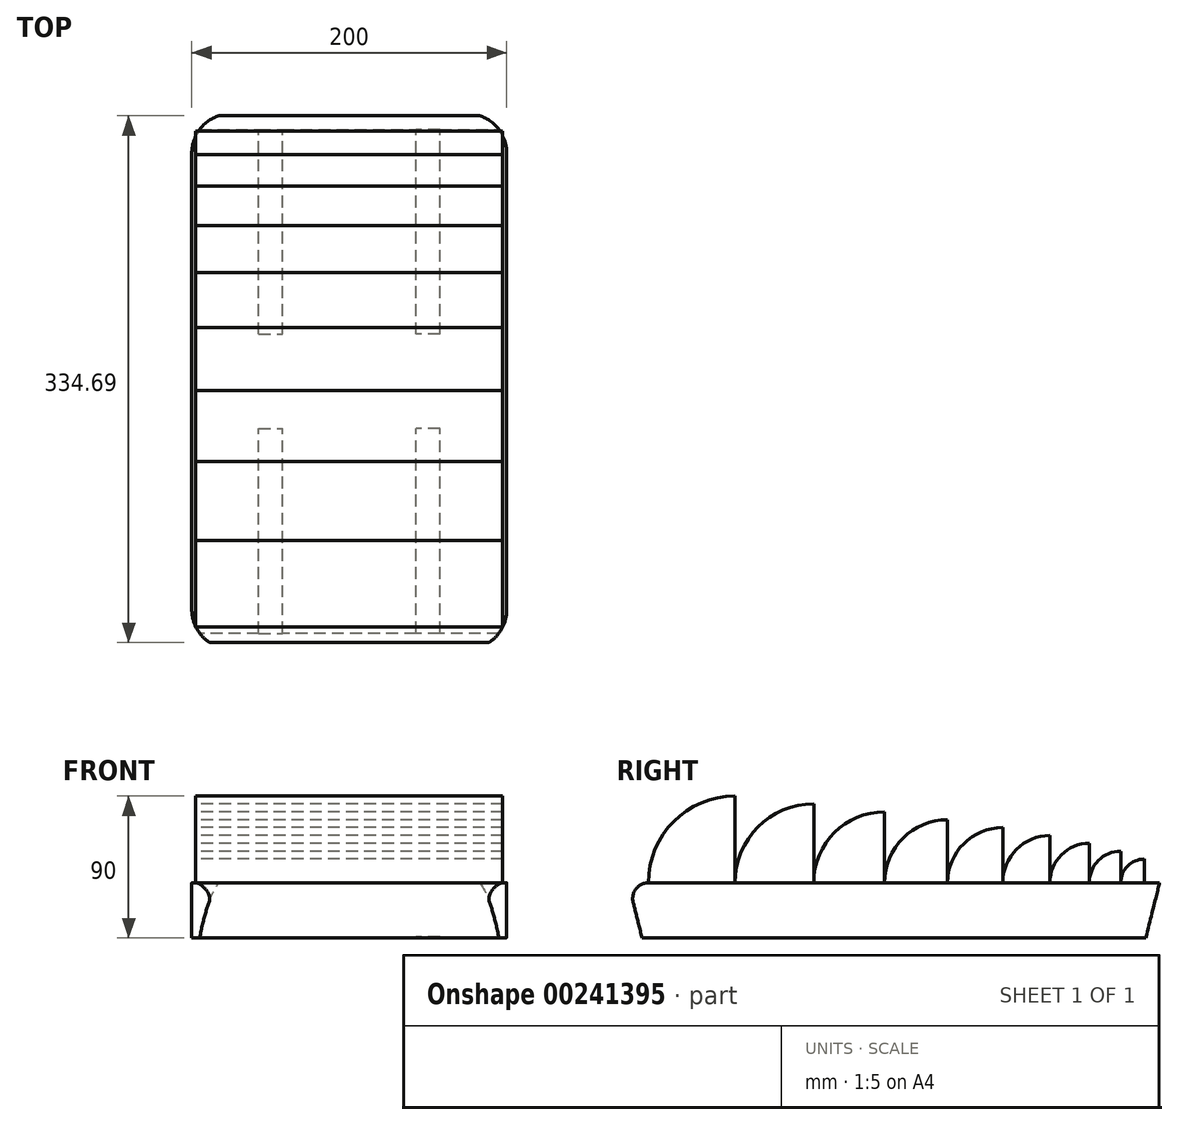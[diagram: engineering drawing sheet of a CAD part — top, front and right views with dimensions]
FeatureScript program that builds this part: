
annotation { "Feature Type Name" : "Feature", "Feature Type Description" : "" }
export const myFeature = defineFeature(function(context is Context, id is Id, definition is map)
    precondition{}
    {
        {
            var Q0;
            Q0=qCreatedBy(makeId("Top.planeOp"),FACE);
            var sketch = newSketch(context, id + "F0", { "sketchPlane" : qUnion([Q0])});
            skLineSegment(sketch, "E0.bottom", {"start": v(-100, 170) * mm, "end": v(100, 170) * mm});
            skLineSegment(sketch, "E0.top", {"start": v(-100, -170) * mm, "end": v(100, -170) * mm});
            skLineSegment(sketch, "E0.left", {"start": v(-100, 170) * mm, "end": v(-100, -170) * mm});
            skLineSegment(sketch, "E0.right", {"start": v(100, 170) * mm, "end": v(100, -170) * mm});
            skPoint(sketch, "E0.middle", {"position": v(0, 0) * mm});
            skSolve(sketch);
        }
        {
            var Q0;
            Q0 = qSketchRegion(id + "F0", true);
            extrude(context, id + "F1", {"entities" : qUnion([Q0]), "depth" : 35 * mm});
        }
        {
            var Q0;
            Q0=makeQuery(id+"F1.opExtrude","CAP_FACE",FACE,{"disambiguationData":[OSD([sQuery(id+"F0.wireOp",EDGE,"E0.bottom"),sQuery(id+"F0.wireOp",EDGE,"E0.top"),sQuery(id+"F0.wireOp",EDGE,"E0.left"),sQuery(id+"F0.wireOp",EDGE,"E0.right")])],"isStart":true});
            var sketch = newSketch(context, id + "F2", { "sketchPlane" : qUnion([Q0])});
            skLineSegment(sketch, "E1.bottom", {"start": v(-57.5, 160) * mm, "end": v(-42.5, 160) * mm});
            skLineSegment(sketch, "E1.top", {"start": v(-57.5, 30) * mm, "end": v(-42.5, 30) * mm});
            skLineSegment(sketch, "E1.left", {"start": v(-57.5, 160) * mm, "end": v(-57.5, 30) * mm});
            skLineSegment(sketch, "E1.right", {"start": v(-42.5, 160) * mm, "end": v(-42.5, 30) * mm});
            skLineSegment(sketch, "E2.bottom", {"start": v(57.5, 160) * mm, "end": v(42.5, 160) * mm});
            skLineSegment(sketch, "E2.top", {"start": v(57.5, 30) * mm, "end": v(42.5, 30) * mm});
            skLineSegment(sketch, "E2.left", {"start": v(57.5, 160) * mm, "end": v(57.5, 30) * mm});
            skLineSegment(sketch, "E2.right", {"start": v(42.5, 160) * mm, "end": v(42.5, 30) * mm});
            skLineSegment(sketch, "E3.bottom", {"start": v(-57.5, -30) * mm, "end": v(-42.5, -30) * mm});
            skLineSegment(sketch, "E3.top", {"start": v(-57.5, -160) * mm, "end": v(-42.5, -160) * mm});
            skLineSegment(sketch, "E3.left", {"start": v(-57.5, -30) * mm, "end": v(-57.5, -160) * mm});
            skLineSegment(sketch, "E3.right", {"start": v(-42.5, -30) * mm, "end": v(-42.5, -160) * mm});
            skLineSegment(sketch, "E4.bottom", {"start": v(57.5, -30) * mm, "end": v(42.5, -30) * mm});
            skLineSegment(sketch, "E4.top", {"start": v(57.5, -160) * mm, "end": v(42.5, -160) * mm});
            skLineSegment(sketch, "E4.left", {"start": v(57.5, -30) * mm, "end": v(57.5, -160) * mm});
            skLineSegment(sketch, "E4.right", {"start": v(42.5, -30) * mm, "end": v(42.5, -160) * mm});
            skSolve(sketch);
        }
        {
            var Q0;
            Q0 = qSketchRegion(id + "F2", true);
            extrude(context, id + "F3", {"entities" : qUnion([Q0]), "operationType" : NewBodyOperationType.REMOVE, "oppositeDirection" : true, "depth" : .5 * mm});
        }
        {
            var Q0;
            Q0=makeQuery(id+"F1.opExtrude","SWEPT_EDGE",EDGE,{"disambiguationData":[OSD([sQuery(id+"F0.wireOp",EDGE,"E0.top"),sQuery(id+"F0.wireOp",EDGE,"E0.right")])]});
            var Q1;
            Q1=makeQuery(id+"F1.opExtrude","SWEPT_EDGE",EDGE,{"disambiguationData":[OSD([sQuery(id+"F0.wireOp",EDGE,"E0.top"),sQuery(id+"F0.wireOp",EDGE,"E0.left")])]});
            var Q2;
            Q2=makeQuery(id+"F1.opExtrude","SWEPT_EDGE",EDGE,{"disambiguationData":[OSD([sQuery(id+"F0.wireOp",EDGE,"E0.bottom"),sQuery(id+"F0.wireOp",EDGE,"E0.right")])]});
            var Q3;
            Q3=makeQuery(id+"F1.opExtrude","SWEPT_EDGE",EDGE,{"disambiguationData":[OSD([sQuery(id+"F0.wireOp",EDGE,"E0.bottom"),sQuery(id+"F0.wireOp",EDGE,"E0.left")])]});
            fillet(context, id + "F4", {"entities" : qUnion([Q0, Q1, Q2, Q3]), "radius" : 25 * mm, "tangentPropagation" : true, "allowEdgeOverflow" : false});
        }
        {
            var Q0;
            Q0=makeQuery(id+"F1.opExtrude","CAP_EDGE",EDGE,{"disambiguationData":[OSD([sQuery(id+"F0.wireOp",EDGE,"E0.top")])],"isStart":true});
            var Q1;
            Q1=makeQuery(id+"F1.opExtrude","CAP_EDGE",EDGE,{"disambiguationData":[OSD([sQuery(id+"F0.wireOp",EDGE,"E0.bottom")])],"isStart":true});
            chamfer(context, id + "F5", {"entities" : qUnion([Q0, Q1]), "chamferType" : ChamferType.TWO_OFFSETS, "width1" : 40 * mm, "oppositeDirection" : false, "width2" : 10 * mm});
        }
        {
            var Q0;
            {var subQ0=sQuery(id+"F0.wireOp",EDGE,"E0.top");Q0=makeQuery(id+"F5.opChamfer","BLEND_EDGE",EDGE,{"blendedFrom":[makeQuery(id+"F1.opExtrude","CAP_EDGE",EDGE,{"disambiguationData":[OSD([subQ0])],"isStart":true}),makeQuery(id+"F1.opExtrude","CAP_FACE",FACE,{"disambiguationData":[OSD([sQuery(id+"F0.wireOp",EDGE,"E0.bottom"),subQ0,sQuery(id+"F0.wireOp",EDGE,"E0.left"),sQuery(id+"F0.wireOp",EDGE,"E0.right")])],"isStart":false})],"blendedInto":[makeQuery(id+"F1.opExtrude","CAP_FACE",FACE,{"disambiguationData":[OSD([sQuery(id+"F0.wireOp",EDGE,"E0.bottom"),subQ0,sQuery(id+"F0.wireOp",EDGE,"E0.left"),sQuery(id+"F0.wireOp",EDGE,"E0.right")])],"isStart":false})]});}
            fillet(context, id + "F6", {"entities" : qUnion([Q0]), "radius" : 10 * mm, "tangentPropagation" : true, "allowEdgeOverflow" : false});
        }
        {
            var Q0;
            Q0=qCreatedBy(makeId("Right.planeOp"),FACE);
            var sketch = newSketch(context, id + "F7", { "sketchPlane" : qUnion([Q0])});
            skLineSegment(sketch, "E5.bottom", {"start": v(-100.94, 35) * mm, "end": v(-155.94, 35) * mm});
            skLineSegment(sketch, "E5.top", {"start": v(-100.94, 90) * mm, "end": v(-100.94, 90) * mm});
            skLineSegment(sketch, "E5.left", {"start": v(-100.94, 35) * mm, "end": v(-100.94, 90) * mm});
            skLineSegment(sketch, "E5.right", {"start": v(-155.94, 35) * mm, "end": v(-155.94, 35) * mm});
            skPoint(sketch, "E6.visualSharp", {"position": v(-155.94, 90) * mm});
            skArc(sketch, "E6.filletArc", {"start": v(-100.94, 90) * mm, "mid": v(-139.83, 73.9) * mm, "end": v(-155.94, 35) * mm});
            skLineSegment(sketch, "E7.bottom", {"start": v(-50.94, 35) * mm, "end": v(-100.94, 35) * mm});
            skLineSegment(sketch, "E7.left", {"start": v(-50.94, 35) * mm, "end": v(-50.94, 85) * mm});
            skArc(sketch, "E8", {"start": v(-50.94, 85) * mm, "mid": v(-86.3, 70.36) * mm, "end": v(-100.94, 35) * mm});
            skLineSegment(sketch, "E9.bottom", {"start": v(-50.94, 35) * mm, "end": v(-5.94, 35) * mm});
            skLineSegment(sketch, "E9.right", {"start": v(-5.94, 35) * mm, "end": v(-5.94, 80) * mm});
            skArc(sketch, "E10", {"start": v(-5.94, 80) * mm, "mid": v(-37.76, 66.82) * mm, "end": v(-50.94, 35) * mm});
            skLineSegment(sketch, "E11.bottom", {"start": v(-5.94, 35) * mm, "end": v(34.06, 35) * mm});
            skLineSegment(sketch, "E11.top", {"start": v(-5.94, 75) * mm, "end": v(34.06, 75) * mm});
            skLineSegment(sketch, "E11.left", {"start": v(-5.94, 35) * mm, "end": v(-5.94, 75) * mm});
            skLineSegment(sketch, "E11.right", {"start": v(34.06, 35) * mm, "end": v(34.06, 75) * mm});
            skArc(sketch, "E12", {"start": v(34.06, 75) * mm, "mid": v(5.77, 63.28) * mm, "end": v(-5.94, 35) * mm});
            skLineSegment(sketch, "E13.bottom", {"start": v(34.06, 35) * mm, "end": v(69.06, 35) * mm});
            skLineSegment(sketch, "E13.top", {"start": v(34.06, 70) * mm, "end": v(69.06, 70) * mm});
            skLineSegment(sketch, "E13.left", {"start": v(34.06, 35) * mm, "end": v(34.06, 70) * mm});
            skLineSegment(sketch, "E13.right", {"start": v(69.06, 35) * mm, "end": v(69.06, 70) * mm});
            skLineSegment(sketch, "E14.bottom", {"start": v(69.06, 35) * mm, "end": v(99.06, 35) * mm});
            skLineSegment(sketch, "E14.top", {"start": v(69.06, 65) * mm, "end": v(99.06, 65) * mm});
            skLineSegment(sketch, "E14.left", {"start": v(69.06, 35) * mm, "end": v(69.06, 65) * mm});
            skLineSegment(sketch, "E14.right", {"start": v(99.06, 35) * mm, "end": v(99.06, 65) * mm});
            skLineSegment(sketch, "E15.bottom", {"start": v(99.06, 35) * mm, "end": v(124.06, 35) * mm});
            skLineSegment(sketch, "E15.top", {"start": v(99.06, 60) * mm, "end": v(124.06, 60) * mm});
            skLineSegment(sketch, "E15.left", {"start": v(99.06, 35) * mm, "end": v(99.06, 60) * mm});
            skLineSegment(sketch, "E15.right", {"start": v(124.06, 35) * mm, "end": v(124.06, 60) * mm});
            skLineSegment(sketch, "E16.bottom", {"start": v(124.06, 35) * mm, "end": v(144.06, 35) * mm});
            skLineSegment(sketch, "E16.top", {"start": v(124.06, 55) * mm, "end": v(144.06, 55) * mm});
            skLineSegment(sketch, "E16.left", {"start": v(124.06, 35) * mm, "end": v(124.06, 55) * mm});
            skLineSegment(sketch, "E16.right", {"start": v(144.06, 35) * mm, "end": v(144.06, 55) * mm});
            skLineSegment(sketch, "E17.bottom", {"start": v(144.06, 35) * mm, "end": v(159.06, 35) * mm});
            skLineSegment(sketch, "E17.top", {"start": v(144.06, 50) * mm, "end": v(159.06, 50) * mm});
            skLineSegment(sketch, "E17.left", {"start": v(144.06, 35) * mm, "end": v(144.06, 50) * mm});
            skLineSegment(sketch, "E17.right", {"start": v(159.06, 35) * mm, "end": v(159.06, 50) * mm});
            skArc(sketch, "E18", {"start": v(69.06, 70) * mm, "mid": v(44.3, 59.75) * mm, "end": v(34.06, 35) * mm});
            skArc(sketch, "E19", {"start": v(99.06, 65) * mm, "mid": v(77.84, 56.21) * mm, "end": v(69.06, 35) * mm});
            skArc(sketch, "E20", {"start": v(124.06, 60) * mm, "mid": v(106.38, 52.68) * mm, "end": v(99.06, 35) * mm});
            skArc(sketch, "E21", {"start": v(144.06, 55) * mm, "mid": v(129.92, 49.14) * mm, "end": v(124.06, 35) * mm});
            skArc(sketch, "E22", {"start": v(159.06, 50) * mm, "mid": v(148.45, 45.6) * mm, "end": v(144.06, 35) * mm});
            skSolve(sketch);
        }
        {
            var Q0;
            Q0=makeQuery(id+"F7.imprint","IMPRINT",FACE,{"disambiguationData":[TD([[makeQuery(id+"F7.imprint","IMPRINT",EDGE,{"derivedFrom":sQuery(id+"F7.wireOp",EDGE,"E5.bottom")}),-1.0]])]});
            var Q1;
            Q1=makeQuery(id+"F7.imprint","IMPRINT",FACE,{"disambiguationData":[TD([[makeQuery(id+"F7.imprint","IMPRINT",EDGE,{"derivedFrom":sQuery(id+"F7.wireOp",EDGE,"E7.bottom")}),-1.0]])]});
            var Q2;
            Q2=makeQuery(id+"F7.imprint","IMPRINT",FACE,{"disambiguationData":[TD([[makeQuery(id+"F7.imprint","IMPRINT",EDGE,{"derivedFrom":sQuery(id+"F7.wireOp",EDGE,"E9.bottom")}),1.0]])]});
            var Q3;
            Q3=makeQuery(id+"F7.imprint","IMPRINT",FACE,{"disambiguationData":[TD([[makeQuery(id+"F7.imprint","IMPRINT",EDGE,{"derivedFrom":sQuery(id+"F7.wireOp",EDGE,"E17.bottom")}),1.0]])]});
            var Q4;
            Q4=makeQuery(id+"F7.imprint","IMPRINT",FACE,{"disambiguationData":[TD([[makeQuery(id+"F7.imprint","IMPRINT",EDGE,{"derivedFrom":sQuery(id+"F7.wireOp",EDGE,"E11.bottom")}),1.0]])]});
            var Q5;
            Q5=makeQuery(id+"F7.imprint","IMPRINT",FACE,{"disambiguationData":[TD([[makeQuery(id+"F7.imprint","IMPRINT",EDGE,{"derivedFrom":sQuery(id+"F7.wireOp",EDGE,"E13.bottom")}),1.0]])]});
            var Q6;
            Q6=makeQuery(id+"F7.imprint","IMPRINT",FACE,{"disambiguationData":[TD([[makeQuery(id+"F7.imprint","IMPRINT",EDGE,{"derivedFrom":sQuery(id+"F7.wireOp",EDGE,"E14.bottom")}),1.0]])]});
            var Q7;
            Q7=makeQuery(id+"F7.imprint","IMPRINT",FACE,{"disambiguationData":[TD([[makeQuery(id+"F7.imprint","IMPRINT",EDGE,{"derivedFrom":sQuery(id+"F7.wireOp",EDGE,"E15.bottom")}),1.0]])]});
            var Q8;
            Q8=makeQuery(id+"F7.imprint","IMPRINT",FACE,{"disambiguationData":[TD([[makeQuery(id+"F7.imprint","IMPRINT",EDGE,{"derivedFrom":sQuery(id+"F7.wireOp",EDGE,"E16.bottom")}),1.0]])]});
            extrude(context, id + "F8", {"entities" : qUnion([Q0, Q1, Q2, Q3, Q4, Q5, Q6, Q7, Q8]), "operationType" : NewBodyOperationType.ADD, "endBound" : BoundingType.SYMMETRIC, "depth" : 194.96 * mm});
        }
    });
